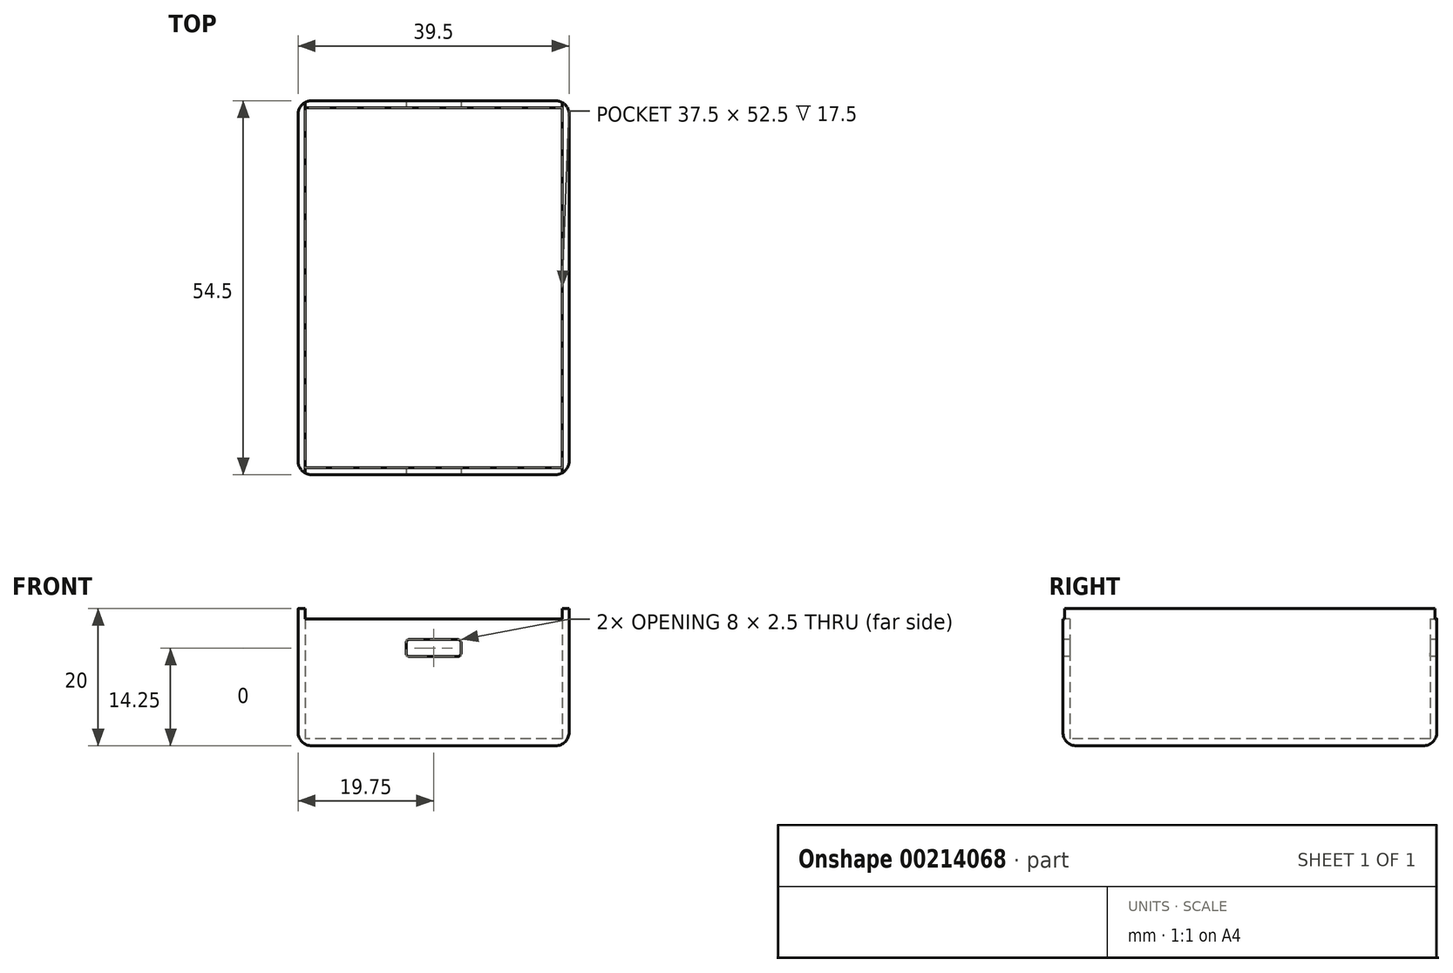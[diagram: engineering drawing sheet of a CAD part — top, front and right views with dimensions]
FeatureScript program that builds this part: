
annotation { "Feature Type Name" : "Feature", "Feature Type Description" : "" }
export const myFeature = defineFeature(function(context is Context, id is Id, definition is map)
    precondition{}
    {
        {
            var Q0;
            Q0=qCreatedBy(makeId("Top.planeOp"),FACE);
            var sketch = newSketch(context, id + "F0", { "sketchPlane" : qUnion([Q0])});
            skLineSegment(sketch, "E0.bottom", {"start": v(18.75, 26.25) * mm, "end": v(-18.75, 26.25) * mm});
            skLineSegment(sketch, "E0.top", {"start": v(18.75, -26.25) * mm, "end": v(-18.75, -26.25) * mm});
            skLineSegment(sketch, "E0.left", {"start": v(18.75, 26.25) * mm, "end": v(18.75, -26.25) * mm});
            skLineSegment(sketch, "E0.right", {"start": v(-18.75, 26.25) * mm, "end": v(-18.75, -26.25) * mm});
            skPoint(sketch, "E0.middle", {"position": v(0, 0) * mm});
            skLineSegment(sketch, "E1.bottom", {"start": v(19.75, 27.25) * mm, "end": v(-19.75, 27.25) * mm});
            skLineSegment(sketch, "E1.top", {"start": v(19.75, -27.25) * mm, "end": v(-19.75, -27.25) * mm});
            skLineSegment(sketch, "E1.left", {"start": v(19.75, 27.25) * mm, "end": v(19.75, -27.25) * mm});
            skLineSegment(sketch, "E1.right", {"start": v(-19.75, 27.25) * mm, "end": v(-19.75, -27.25) * mm});
            skLineSegment(sketch, "E2", {"start": v(18.75, 26.25) * mm, "end": v(18.75, 27.25) * mm});
            skLineSegment(sketch, "E3", {"start": v(18.75, -26.25) * mm, "end": v(18.75, -27.25) * mm});
            skLineSegment(sketch, "E4", {"start": v(-18.75, 26.25) * mm, "end": v(-18.75, 27.25) * mm});
            skLineSegment(sketch, "E5", {"start": v(-18.75, -26.25) * mm, "end": v(-18.75, -27.25) * mm});
            skSolve(sketch);
        }
        {
            var Q0;
            Q0=makeQuery(id+"F0.imprint","IMPRINT",FACE,{"disambiguationData":[TD([[makeQuery(id+"F0.imprint","IMPRINT",EDGE,{"derivedFrom":sQuery(id+"F0.wireOp",EDGE,"E0.bottom")}),1.0]])]});
            extrude(context, id + "F1", {"entities" : qUnion([Q0]), "depth" : 1 * mm});
        }
        {
            var Q0;
            Q0=makeQuery(id+"F0.imprint","IMPRINT",FACE,{"disambiguationData":[TD([[makeQuery(id+"F0.imprint","IMPRINT",EDGE,{"derivedFrom":sQuery(id+"F0.wireOp",EDGE,"E0.bottom")}),-1.0]])]});
            var Q1;
            Q1=makeQuery(id+"F0.imprint","IMPRINT",FACE,{"disambiguationData":[TD([[makeQuery(id+"F0.imprint","IMPRINT",EDGE,{"derivedFrom":sQuery(id+"F0.wireOp",EDGE,"E0.top")}),1.0]])]});
            extrude(context, id + "F2", {"entities" : qUnion([Q0, Q1]), "operationType" : NewBodyOperationType.ADD, "depth" : 18.5 * mm});
        }
        {
            var Q0;
            Q0=makeQuery(id+"F2.opExtrude","SWEPT_FACE",FACE,{"disambiguationData":[OSD([sQuery(id+"F0.wireOp",EDGE,"E1.top")])]});
            var sketch = newSketch(context, id + "F3", { "sketchPlane" : qUnion([Q0])});
            skLineSegment(sketch, "E6.bottom", {"start": v(3.5, 15.5) * mm, "end": v(-3.5, 15.5) * mm});
            skLineSegment(sketch, "E6.top", {"start": v(3.5, 13) * mm, "end": v(-3.5, 13) * mm});
            skLineSegment(sketch, "E6.left", {"start": v(4, 15) * mm, "end": v(4, 13.5) * mm});
            skLineSegment(sketch, "E6.right", {"start": v(-4, 15) * mm, "end": v(-4, 13.5) * mm});
            skPoint(sketch, "E6.middle", {"position": v(0, 14.25) * mm});
            skPoint(sketch, "E7.visualSharp", {"position": v(-4, 15.5) * mm});
            skArc(sketch, "E7.filletArc", {"start": v(-3.5, 15.5) * mm, "mid": v(-3.85, 15.35) * mm, "end": v(-4, 15) * mm});
            skPoint(sketch, "E8.visualSharp", {"position": v(-4, 13) * mm});
            skArc(sketch, "E8.filletArc", {"start": v(-4, 13.5) * mm, "mid": v(-3.85, 13.15) * mm, "end": v(-3.5, 13) * mm});
            skPoint(sketch, "E9.visualSharp", {"position": v(4, 13) * mm});
            skArc(sketch, "E9.filletArc", {"start": v(3.5, 13) * mm, "mid": v(3.85, 13.15) * mm, "end": v(4, 13.5) * mm});
            skPoint(sketch, "E10.visualSharp", {"position": v(4, 15.5) * mm});
            skArc(sketch, "E10.filletArc", {"start": v(4, 15) * mm, "mid": v(3.85, 15.35) * mm, "end": v(3.5, 15.5) * mm});
            skSolve(sketch);
        }
        {
            var Q0;
            Q0=makeQuery(id+"F3.imprint","IMPRINT",FACE,{"disambiguationData":[TD([[makeQuery(id+"F3.imprint","IMPRINT",EDGE,{"derivedFrom":sQuery(id+"F3.wireOp",EDGE,"E6.bottom")}),1.0]])]});
            extrude(context, id + "F4", {"entities" : qUnion([Q0]), "operationType" : NewBodyOperationType.REMOVE, "oppositeDirection" : true, "depth" : 60 * mm});
        }
        {
            var Q0;
            Q0=makeQuery(id+"F0.imprint","IMPRINT",FACE,{"disambiguationData":[TD([[makeQuery(id+"F0.imprint","IMPRINT",EDGE,{"derivedFrom":sQuery(id+"F0.wireOp",EDGE,"E0.right")}),-1.0]])]});
            var Q1;
            Q1=makeQuery(id+"F0.imprint","IMPRINT",FACE,{"disambiguationData":[TD([[makeQuery(id+"F0.imprint","IMPRINT",EDGE,{"derivedFrom":sQuery(id+"F0.wireOp",EDGE,"E0.left")}),1.0]])]});
            extrude(context, id + "F5", {"entities" : qUnion([Q0, Q1]), "operationType" : NewBodyOperationType.ADD, "depth" : 20 * mm});
        }
        {
            var Q0;
            Q0=makeQuery(id+"F5.opExtrude","SWEPT_EDGE",EDGE,{"disambiguationData":[OSD([sQuery(id+"F0.wireOp",EDGE,"E1.top"),sQuery(id+"F0.wireOp",EDGE,"E1.left")])]});
            var Q1;
            Q1=makeQuery(id+"F5.opExtrude","SWEPT_EDGE",EDGE,{"disambiguationData":[OSD([sQuery(id+"F0.wireOp",EDGE,"E1.top"),sQuery(id+"F0.wireOp",EDGE,"E1.right")])]});
            var Q2;
            Q2=makeQuery(id+"F5.opExtrude","SWEPT_EDGE",EDGE,{"disambiguationData":[OSD([sQuery(id+"F0.wireOp",EDGE,"E1.bottom"),sQuery(id+"F0.wireOp",EDGE,"E1.left")])]});
            var Q3;
            Q3=makeQuery(id+"F5.opExtrude","SWEPT_EDGE",EDGE,{"disambiguationData":[OSD([sQuery(id+"F0.wireOp",EDGE,"E1.bottom"),sQuery(id+"F0.wireOp",EDGE,"E1.right")])]});
            fillet(context, id + "F6", {"entities" : qUnion([Q0, Q1, Q2, Q3]), "radius" : 2 * mm, "tangentPropagation" : true, "allowEdgeOverflow" : false});
        }
        {
            var Q0;
            Q0=makeQuery(id+"F5.opExtrude","CAP_EDGE",EDGE,{"disambiguationData":[OSD([sQuery(id+"F0.wireOp",EDGE,"E1.right")])],"isStart":true});
            var Q1;
            {var subQ0=sQuery(id+"F0.wireOp",EDGE,"E5");var subQ1=sQuery(id+"F0.wireOp",EDGE,"E4");var subQ2=sQuery(id+"F0.wireOp",EDGE,"E1.right");var subQ3=sQuery(id+"F0.wireOp",EDGE,"E1.top");var subQ4=sQuery(id+"F0.wireOp",EDGE,"E1.bottom");var subQ5=sQuery(id+"F0.wireOp",EDGE,"E0.right");var subQ6=sQuery(id+"F0.wireOp",EDGE,"E3");var subQ7=sQuery(id+"F0.wireOp",EDGE,"E2");var subQ8=sQuery(id+"F0.wireOp",EDGE,"E0.left");var subQ9=sQuery(id+"F0.wireOp",EDGE,"E0.top");var subQ10=sQuery(id+"F0.wireOp",EDGE,"E0.bottom");Q1=makeQuery(id+"F6.opFillet","BLEND_EDGE",EDGE,{"blendedFrom":[makeQuery(id+"F5.opExtrude","SWEPT_EDGE",EDGE,{"disambiguationData":[OSD([subQ3,subQ2])]}),makeQuery(id+"F5.boolean.opBoolean","MERGE",FACE,{"derivedFrom":[makeQuery(id+"F2.boolean.opBoolean","MERGE",FACE,{"derivedFrom":[makeQuery(id+"F1.opExtrude","CAP_FACE",FACE,{"disambiguationData":[OSD([subQ10,subQ9,subQ8,subQ5])],"isStart":true}),makeQuery(id+"F2.opExtrude","CAP_FACE",FACE,{"disambiguationData":[OSD([subQ10,subQ4,subQ7,subQ1])],"isStart":true}),makeQuery(id+"F2.opExtrude","CAP_FACE",FACE,{"disambiguationData":[OSD([subQ9,subQ3,subQ6,subQ0])],"isStart":true})]}),makeQuery(id+"F5.opExtrude","CAP_FACE",FACE,{"disambiguationData":[OSD([subQ8,subQ4,subQ3,sQuery(id+"F0.wireOp",EDGE,"E1.left"),subQ7,subQ6])],"isStart":true}),makeQuery(id+"F5.opExtrude","CAP_FACE",FACE,{"disambiguationData":[OSD([subQ5,subQ4,subQ3,subQ2,subQ1,subQ0])],"isStart":true})]})],"blendedInto":[makeQuery(id+"F5.boolean.opBoolean","MERGE",FACE,{"derivedFrom":[makeQuery(id+"F2.boolean.opBoolean","MERGE",FACE,{"derivedFrom":[makeQuery(id+"F1.opExtrude","CAP_FACE",FACE,{"disambiguationData":[OSD([subQ10,subQ9,subQ8,subQ5])],"isStart":true}),makeQuery(id+"F2.opExtrude","CAP_FACE",FACE,{"disambiguationData":[OSD([subQ10,subQ4,subQ7,subQ1])],"isStart":true}),makeQuery(id+"F2.opExtrude","CAP_FACE",FACE,{"disambiguationData":[OSD([subQ9,subQ3,subQ6,subQ0])],"isStart":true})]}),makeQuery(id+"F5.opExtrude","CAP_FACE",FACE,{"disambiguationData":[OSD([subQ8,subQ4,subQ3,sQuery(id+"F0.wireOp",EDGE,"E1.left"),subQ7,subQ6])],"isStart":true}),makeQuery(id+"F5.opExtrude","CAP_FACE",FACE,{"disambiguationData":[OSD([subQ5,subQ4,subQ3,subQ2,subQ1,subQ0])],"isStart":true})]})]});}
            var Q2;
            {var subQ0=sQuery(id+"F0.wireOp",EDGE,"E1.top");Q2=makeQuery(id+"F5.boolean.opBoolean","MERGE",EDGE,{"derivedFrom":[makeQuery(id+"F2.opExtrude","CAP_EDGE",EDGE,{"disambiguationData":[OSD([subQ0])],"isStart":true}),makeQuery(id+"F5.opExtrude","CAP_EDGE",EDGE,{"disambiguationData":[OSD([subQ0]),TDD([makeQuery(id+"F0.imprint","IMPRINT",EDGE,{"disambiguationData":[TD([[makeQuery(id+"F0.imprint","INTERSECT",VERTEX,{"derivedFrom":[subQ0,sQuery(id+"F0.wireOp",EDGE,"E1.left")]}),-1.0]])],"derivedFrom":subQ0})])],"isStart":true}),makeQuery(id+"F5.opExtrude","CAP_EDGE",EDGE,{"disambiguationData":[OSD([subQ0]),TDD([makeQuery(id+"F0.imprint","IMPRINT",EDGE,{"disambiguationData":[TD([[makeQuery(id+"F0.imprint","INTERSECT",VERTEX,{"derivedFrom":[subQ0,sQuery(id+"F0.wireOp",EDGE,"E1.right")]}),1.0]])],"derivedFrom":subQ0})])],"isStart":true})]});}
            var Q3;
            {var subQ0=sQuery(id+"F0.wireOp",EDGE,"E5");var subQ1=sQuery(id+"F0.wireOp",EDGE,"E4");var subQ2=sQuery(id+"F0.wireOp",EDGE,"E1.top");var subQ3=sQuery(id+"F0.wireOp",EDGE,"E1.bottom");var subQ4=sQuery(id+"F0.wireOp",EDGE,"E0.right");var subQ5=sQuery(id+"F0.wireOp",EDGE,"E3");var subQ6=sQuery(id+"F0.wireOp",EDGE,"E2");var subQ7=sQuery(id+"F0.wireOp",EDGE,"E1.left");var subQ8=sQuery(id+"F0.wireOp",EDGE,"E0.left");var subQ9=sQuery(id+"F0.wireOp",EDGE,"E0.top");var subQ10=sQuery(id+"F0.wireOp",EDGE,"E0.bottom");Q3=makeQuery(id+"F6.opFillet","BLEND_EDGE",EDGE,{"blendedFrom":[makeQuery(id+"F5.opExtrude","SWEPT_EDGE",EDGE,{"disambiguationData":[OSD([subQ2,subQ7])]}),makeQuery(id+"F5.boolean.opBoolean","MERGE",FACE,{"derivedFrom":[makeQuery(id+"F2.boolean.opBoolean","MERGE",FACE,{"derivedFrom":[makeQuery(id+"F1.opExtrude","CAP_FACE",FACE,{"disambiguationData":[OSD([subQ10,subQ9,subQ8,subQ4])],"isStart":true}),makeQuery(id+"F2.opExtrude","CAP_FACE",FACE,{"disambiguationData":[OSD([subQ10,subQ3,subQ6,subQ1])],"isStart":true}),makeQuery(id+"F2.opExtrude","CAP_FACE",FACE,{"disambiguationData":[OSD([subQ9,subQ2,subQ5,subQ0])],"isStart":true})]}),makeQuery(id+"F5.opExtrude","CAP_FACE",FACE,{"disambiguationData":[OSD([subQ8,subQ3,subQ2,subQ7,subQ6,subQ5])],"isStart":true}),makeQuery(id+"F5.opExtrude","CAP_FACE",FACE,{"disambiguationData":[OSD([subQ4,subQ3,subQ2,sQuery(id+"F0.wireOp",EDGE,"E1.right"),subQ1,subQ0])],"isStart":true})]})],"blendedInto":[makeQuery(id+"F5.boolean.opBoolean","MERGE",FACE,{"derivedFrom":[makeQuery(id+"F2.boolean.opBoolean","MERGE",FACE,{"derivedFrom":[makeQuery(id+"F1.opExtrude","CAP_FACE",FACE,{"disambiguationData":[OSD([subQ10,subQ9,subQ8,subQ4])],"isStart":true}),makeQuery(id+"F2.opExtrude","CAP_FACE",FACE,{"disambiguationData":[OSD([subQ10,subQ3,subQ6,subQ1])],"isStart":true}),makeQuery(id+"F2.opExtrude","CAP_FACE",FACE,{"disambiguationData":[OSD([subQ9,subQ2,subQ5,subQ0])],"isStart":true})]}),makeQuery(id+"F5.opExtrude","CAP_FACE",FACE,{"disambiguationData":[OSD([subQ8,subQ3,subQ2,subQ7,subQ6,subQ5])],"isStart":true}),makeQuery(id+"F5.opExtrude","CAP_FACE",FACE,{"disambiguationData":[OSD([subQ4,subQ3,subQ2,sQuery(id+"F0.wireOp",EDGE,"E1.right"),subQ1,subQ0])],"isStart":true})]})]});}
            var Q4;
            Q4=makeQuery(id+"F5.opExtrude","CAP_EDGE",EDGE,{"disambiguationData":[OSD([sQuery(id+"F0.wireOp",EDGE,"E1.left")])],"isStart":true});
            var Q5;
            {var subQ0=sQuery(id+"F0.wireOp",EDGE,"E5");var subQ1=sQuery(id+"F0.wireOp",EDGE,"E4");var subQ2=sQuery(id+"F0.wireOp",EDGE,"E1.top");var subQ3=sQuery(id+"F0.wireOp",EDGE,"E1.bottom");var subQ4=sQuery(id+"F0.wireOp",EDGE,"E0.right");var subQ5=sQuery(id+"F0.wireOp",EDGE,"E3");var subQ6=sQuery(id+"F0.wireOp",EDGE,"E2");var subQ7=sQuery(id+"F0.wireOp",EDGE,"E1.left");var subQ8=sQuery(id+"F0.wireOp",EDGE,"E0.left");var subQ9=sQuery(id+"F0.wireOp",EDGE,"E0.top");var subQ10=sQuery(id+"F0.wireOp",EDGE,"E0.bottom");Q5=makeQuery(id+"F6.opFillet","BLEND_EDGE",EDGE,{"blendedFrom":[makeQuery(id+"F5.opExtrude","SWEPT_EDGE",EDGE,{"disambiguationData":[OSD([subQ3,subQ7])]}),makeQuery(id+"F5.boolean.opBoolean","MERGE",FACE,{"derivedFrom":[makeQuery(id+"F2.boolean.opBoolean","MERGE",FACE,{"derivedFrom":[makeQuery(id+"F1.opExtrude","CAP_FACE",FACE,{"disambiguationData":[OSD([subQ10,subQ9,subQ8,subQ4])],"isStart":true}),makeQuery(id+"F2.opExtrude","CAP_FACE",FACE,{"disambiguationData":[OSD([subQ10,subQ3,subQ6,subQ1])],"isStart":true}),makeQuery(id+"F2.opExtrude","CAP_FACE",FACE,{"disambiguationData":[OSD([subQ9,subQ2,subQ5,subQ0])],"isStart":true})]}),makeQuery(id+"F5.opExtrude","CAP_FACE",FACE,{"disambiguationData":[OSD([subQ8,subQ3,subQ2,subQ7,subQ6,subQ5])],"isStart":true}),makeQuery(id+"F5.opExtrude","CAP_FACE",FACE,{"disambiguationData":[OSD([subQ4,subQ3,subQ2,sQuery(id+"F0.wireOp",EDGE,"E1.right"),subQ1,subQ0])],"isStart":true})]})],"blendedInto":[makeQuery(id+"F5.boolean.opBoolean","MERGE",FACE,{"derivedFrom":[makeQuery(id+"F2.boolean.opBoolean","MERGE",FACE,{"derivedFrom":[makeQuery(id+"F1.opExtrude","CAP_FACE",FACE,{"disambiguationData":[OSD([subQ10,subQ9,subQ8,subQ4])],"isStart":true}),makeQuery(id+"F2.opExtrude","CAP_FACE",FACE,{"disambiguationData":[OSD([subQ10,subQ3,subQ6,subQ1])],"isStart":true}),makeQuery(id+"F2.opExtrude","CAP_FACE",FACE,{"disambiguationData":[OSD([subQ9,subQ2,subQ5,subQ0])],"isStart":true})]}),makeQuery(id+"F5.opExtrude","CAP_FACE",FACE,{"disambiguationData":[OSD([subQ8,subQ3,subQ2,subQ7,subQ6,subQ5])],"isStart":true}),makeQuery(id+"F5.opExtrude","CAP_FACE",FACE,{"disambiguationData":[OSD([subQ4,subQ3,subQ2,sQuery(id+"F0.wireOp",EDGE,"E1.right"),subQ1,subQ0])],"isStart":true})]})]});}
            var Q6;
            {var subQ0=sQuery(id+"F0.wireOp",EDGE,"E1.bottom");Q6=makeQuery(id+"F5.boolean.opBoolean","MERGE",EDGE,{"derivedFrom":[makeQuery(id+"F2.opExtrude","CAP_EDGE",EDGE,{"disambiguationData":[OSD([subQ0])],"isStart":true}),makeQuery(id+"F5.opExtrude","CAP_EDGE",EDGE,{"disambiguationData":[OSD([subQ0]),TDD([makeQuery(id+"F0.imprint","IMPRINT",EDGE,{"disambiguationData":[TD([[makeQuery(id+"F0.imprint","INTERSECT",VERTEX,{"derivedFrom":[subQ0,sQuery(id+"F0.wireOp",EDGE,"E1.left")]}),-1.0]])],"derivedFrom":subQ0})])],"isStart":true}),makeQuery(id+"F5.opExtrude","CAP_EDGE",EDGE,{"disambiguationData":[OSD([subQ0]),TDD([makeQuery(id+"F0.imprint","IMPRINT",EDGE,{"disambiguationData":[TD([[makeQuery(id+"F0.imprint","INTERSECT",VERTEX,{"derivedFrom":[subQ0,sQuery(id+"F0.wireOp",EDGE,"E1.right")]}),1.0]])],"derivedFrom":subQ0})])],"isStart":true})]});}
            var Q7;
            {var subQ0=sQuery(id+"F0.wireOp",EDGE,"E5");var subQ1=sQuery(id+"F0.wireOp",EDGE,"E4");var subQ2=sQuery(id+"F0.wireOp",EDGE,"E1.right");var subQ3=sQuery(id+"F0.wireOp",EDGE,"E1.top");var subQ4=sQuery(id+"F0.wireOp",EDGE,"E1.bottom");var subQ5=sQuery(id+"F0.wireOp",EDGE,"E0.right");var subQ6=sQuery(id+"F0.wireOp",EDGE,"E3");var subQ7=sQuery(id+"F0.wireOp",EDGE,"E2");var subQ8=sQuery(id+"F0.wireOp",EDGE,"E0.left");var subQ9=sQuery(id+"F0.wireOp",EDGE,"E0.top");var subQ10=sQuery(id+"F0.wireOp",EDGE,"E0.bottom");Q7=makeQuery(id+"F6.opFillet","BLEND_EDGE",EDGE,{"blendedFrom":[makeQuery(id+"F5.opExtrude","SWEPT_EDGE",EDGE,{"disambiguationData":[OSD([subQ4,subQ2])]}),makeQuery(id+"F5.boolean.opBoolean","MERGE",FACE,{"derivedFrom":[makeQuery(id+"F2.boolean.opBoolean","MERGE",FACE,{"derivedFrom":[makeQuery(id+"F1.opExtrude","CAP_FACE",FACE,{"disambiguationData":[OSD([subQ10,subQ9,subQ8,subQ5])],"isStart":true}),makeQuery(id+"F2.opExtrude","CAP_FACE",FACE,{"disambiguationData":[OSD([subQ10,subQ4,subQ7,subQ1])],"isStart":true}),makeQuery(id+"F2.opExtrude","CAP_FACE",FACE,{"disambiguationData":[OSD([subQ9,subQ3,subQ6,subQ0])],"isStart":true})]}),makeQuery(id+"F5.opExtrude","CAP_FACE",FACE,{"disambiguationData":[OSD([subQ8,subQ4,subQ3,sQuery(id+"F0.wireOp",EDGE,"E1.left"),subQ7,subQ6])],"isStart":true}),makeQuery(id+"F5.opExtrude","CAP_FACE",FACE,{"disambiguationData":[OSD([subQ5,subQ4,subQ3,subQ2,subQ1,subQ0])],"isStart":true})]})],"blendedInto":[makeQuery(id+"F5.boolean.opBoolean","MERGE",FACE,{"derivedFrom":[makeQuery(id+"F2.boolean.opBoolean","MERGE",FACE,{"derivedFrom":[makeQuery(id+"F1.opExtrude","CAP_FACE",FACE,{"disambiguationData":[OSD([subQ10,subQ9,subQ8,subQ5])],"isStart":true}),makeQuery(id+"F2.opExtrude","CAP_FACE",FACE,{"disambiguationData":[OSD([subQ10,subQ4,subQ7,subQ1])],"isStart":true}),makeQuery(id+"F2.opExtrude","CAP_FACE",FACE,{"disambiguationData":[OSD([subQ9,subQ3,subQ6,subQ0])],"isStart":true})]}),makeQuery(id+"F5.opExtrude","CAP_FACE",FACE,{"disambiguationData":[OSD([subQ8,subQ4,subQ3,sQuery(id+"F0.wireOp",EDGE,"E1.left"),subQ7,subQ6])],"isStart":true}),makeQuery(id+"F5.opExtrude","CAP_FACE",FACE,{"disambiguationData":[OSD([subQ5,subQ4,subQ3,subQ2,subQ1,subQ0])],"isStart":true})]})]});}
            fillet(context, id + "F7", {"entities" : qUnion([Q0, Q1, Q2, Q3, Q4, Q5, Q6, Q7]), "radius" : 2 * mm, "tangentPropagation" : true, "allowEdgeOverflow" : false});
        }
    });
